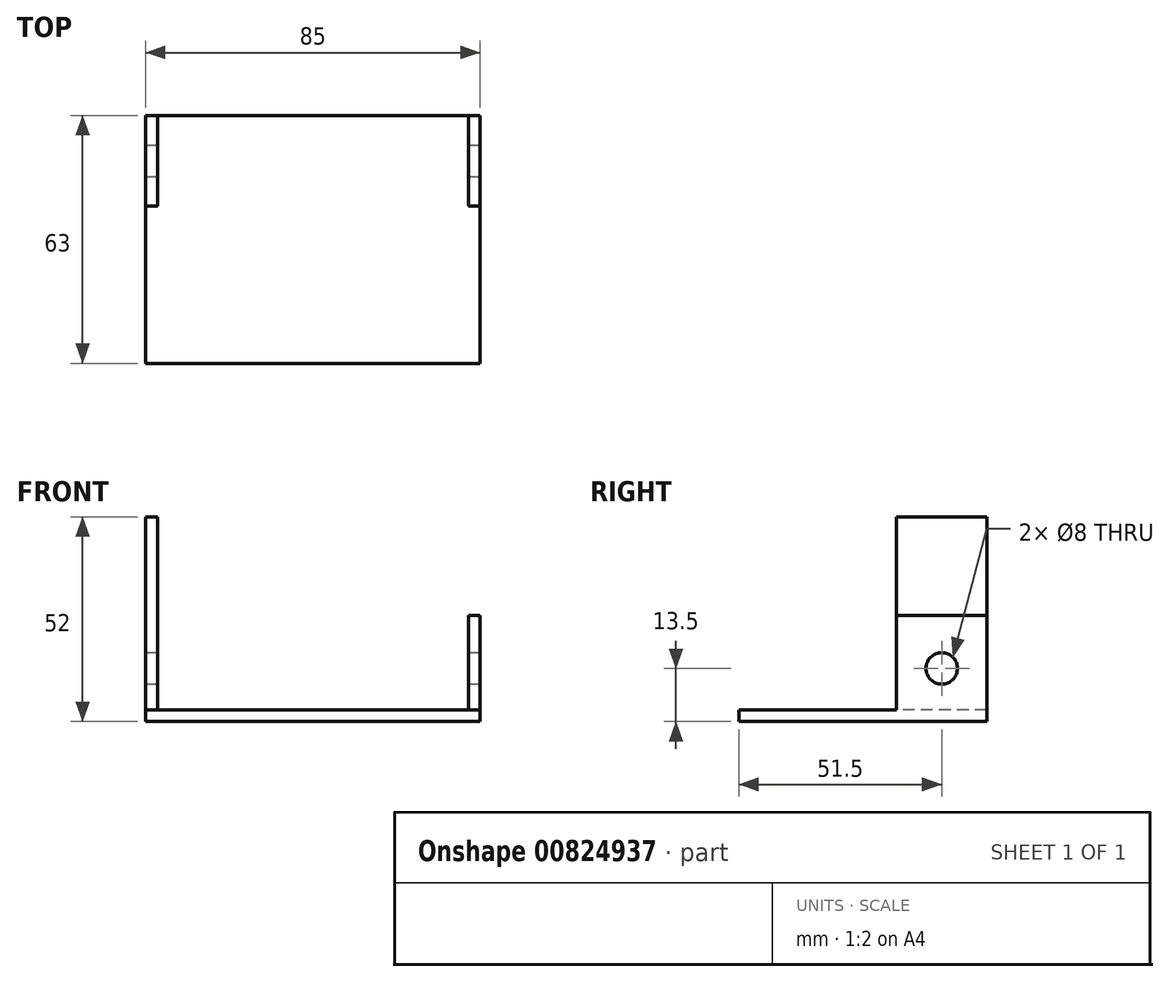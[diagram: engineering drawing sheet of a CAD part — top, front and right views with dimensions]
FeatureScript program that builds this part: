
annotation { "Feature Type Name" : "Feature", "Feature Type Description" : "" }
export const myFeature = defineFeature(function(context is Context, id is Id, definition is map)
    precondition{}
    {
        {
            var Q0;
            Q0=qCreatedBy(makeId("Top.planeOp"),FACE);
            var sketch = newSketch(context, id + "F0", { "sketchPlane" : qUnion([Q0])});
            skLineSegment(sketch, "E0.bottom", {"start": v(0, 0) * mm, "end": v(85, 0) * mm});
            skLineSegment(sketch, "E0.top", {"start": v(0, 23) * mm, "end": v(85, 23) * mm});
            skLineSegment(sketch, "E0.left", {"start": v(0, 0) * mm, "end": v(0, 23) * mm});
            skLineSegment(sketch, "E0.right", {"start": v(85, 0) * mm, "end": v(85, 23) * mm});
            skLineSegment(sketch, "E1.top", {"start": v(0, -40) * mm, "end": v(85, -40) * mm});
            skLineSegment(sketch, "E1.left", {"start": v(0, 0) * mm, "end": v(0, -40) * mm});
            skLineSegment(sketch, "E1.right", {"start": v(85, 0) * mm, "end": v(85, -40) * mm});
            skSolve(sketch);
        }
        {
            var Q0;
            Q0=qSketchRegion(id+"F0",true);
            extrude(context, id + "F1", {"entities" : qUnion([Q0]), "depth" : 3 * mm, "offsetDistance" : 25 * mm});
        }
        {
            var Q0;
            Q0=makeQuery(id+"F1.opExtrude","CAP_FACE",FACE,{"disambiguationData":[OSD([sQuery(id+"F0.wireOp",EDGE,"E0.bottom"),sQuery(id+"F0.wireOp",EDGE,"E0.top"),sQuery(id+"F0.wireOp",EDGE,"E0.left"),sQuery(id+"F0.wireOp",EDGE,"E0.right")])],"isStart":false});
            var sketch = newSketch(context, id + "F2", { "sketchPlane" : qUnion([Q0])});
            skLineSegment(sketch, "E2.bottom", {"start": v(0, 23) * mm, "end": v(3, 23) * mm});
            skLineSegment(sketch, "E2.top", {"start": v(0, 0) * mm, "end": v(3, 0) * mm});
            skLineSegment(sketch, "E2.left", {"start": v(0, 23) * mm, "end": v(0, 0) * mm});
            skLineSegment(sketch, "E2.right", {"start": v(3, 23) * mm, "end": v(3, 0) * mm});
            skLineSegment(sketch, "E3.bottom", {"start": v(85, 23) * mm, "end": v(82, 23) * mm});
            skLineSegment(sketch, "E3.top", {"start": v(85, 0) * mm, "end": v(82, 0) * mm});
            skLineSegment(sketch, "E3.left", {"start": v(85, 23) * mm, "end": v(85, 0) * mm});
            skLineSegment(sketch, "E3.right", {"start": v(82, 23) * mm, "end": v(82, 0) * mm});
            skSolve(sketch);
        }
        {
            var Q0;
            Q0=qSketchRegion(id+"F2",true);
            extrude(context, id + "F3", {"entities" : qUnion([Q0]), "operationType" : NewBodyOperationType.ADD, "depth" : 24 * mm, "offsetDistance" : 25 * mm});
        }
        {
            var Q0;
            Q0=makeQuery(id+"F3.opExtrude","CAP_FACE",FACE,{"disambiguationData":[OSD([sQuery(id+"F2.wireOp",EDGE,"E2.bottom"),sQuery(id+"F2.wireOp",EDGE,"E2.top"),sQuery(id+"F2.wireOp",EDGE,"E2.left"),sQuery(id+"F2.wireOp",EDGE,"E2.right")])],"isStart":false});
            var sketch = newSketch(context, id + "F4", { "sketchPlane" : qUnion([Q0])});
            skLineSegment(sketch, "E4.bottom", {"start": v(0, 23) * mm, "end": v(3, 23) * mm});
            skLineSegment(sketch, "E4.top", {"start": v(0, 0) * mm, "end": v(3, 0) * mm});
            skLineSegment(sketch, "E4.left", {"start": v(0, 23) * mm, "end": v(0, 0) * mm});
            skLineSegment(sketch, "E4.right", {"start": v(3, 23) * mm, "end": v(3, 0) * mm});
            skSolve(sketch);
        }
        {
            var Q0;
            Q0=qSketchRegion(id+"F4",true);
            extrude(context, id + "F5", {"entities" : qUnion([Q0]), "operationType" : NewBodyOperationType.ADD, "depth" : 25 * mm, "offsetDistance" : 25 * mm});
        }
        {
            var Q0;
            Q0=makeQuery(id+"F3.boolean.opBoolean","MERGE",FACE,{"derivedFrom":[makeQuery(id+"F1.opExtrude","SWEPT_FACE",FACE,{"disambiguationData":[OSD([sQuery(id+"F0.wireOp",EDGE,"E0.right"),sQuery(id+"F0.wireOp",EDGE,"E1.right")])]}),makeQuery(id+"F3.opExtrude","SWEPT_FACE",FACE,{"disambiguationData":[OSD([sQuery(id+"F2.wireOp",EDGE,"E3.left")])]})]});
            var sketch = newSketch(context, id + "F6", { "sketchPlane" : qUnion([Q0])});
            skLineSegment(sketch, "E5", {"start": v(0, 27) * mm, "end": v(23, 0) * mm, "construction": true});
            skLineSegment(sketch, "E6", {"start": v(23, 0) * mm, "end": v(23, 27) * mm, "construction": true});
            skLineSegment(sketch, "E7", {"start": v(23, 27) * mm, "end": v(0, 0) * mm, "construction": true});
            skCircle(sketch, "E8", {"center": v(11.5, 13.5) * mm, "radius": 4 * mm});
            skSolve(sketch);
        }
        {
            var Q0;
            Q0=qSketchRegion(id+"F6",true);
            extrude(context, id + "F7", {"entities" : qUnion([Q0]), "operationType" : NewBodyOperationType.REMOVE, "oppositeDirection" : true, "depth" : 200 * mm, "offsetDistance" : 25 * mm});
        }
    });
